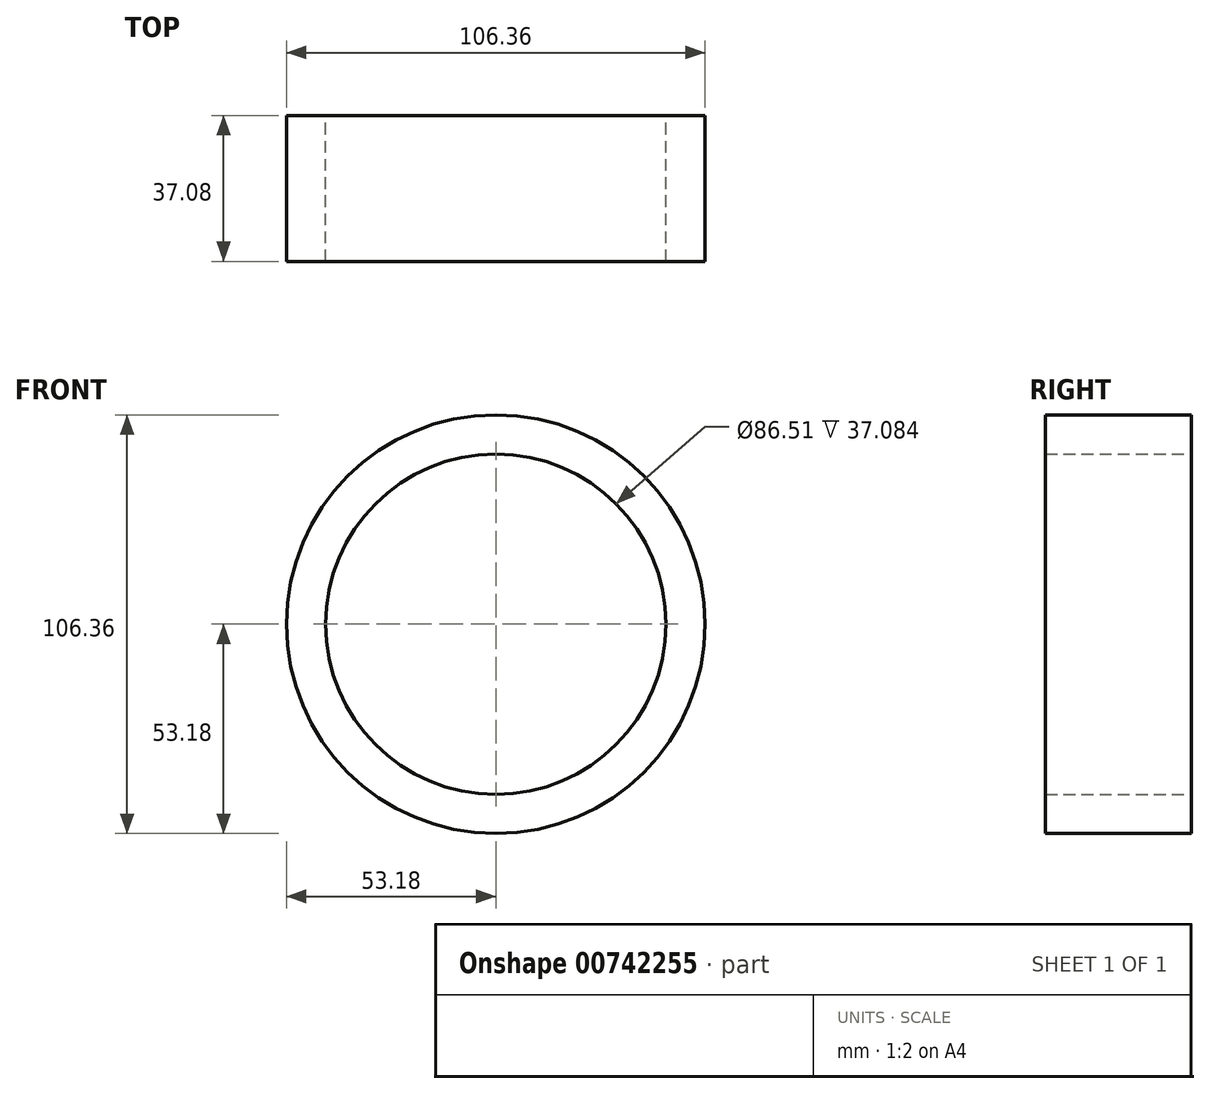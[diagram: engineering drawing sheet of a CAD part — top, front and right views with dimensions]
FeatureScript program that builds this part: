
annotation { "Feature Type Name" : "Feature", "Feature Type Description" : "" }
export const myFeature = defineFeature(function(context is Context, id is Id, definition is map)
    precondition{}
    {
        {
            var Q0;
            Q0=qCreatedBy(makeId("Front.planeOp"),FACE);
            var sketch = newSketch(context, id + "F0", { "sketchPlane" : qUnion([Q0])});
            skCircle(sketch, "E0", {"center": v(0, 0) * mm, "radius": 53.18 * mm});
            skCircle(sketch, "E1", {"center": v(0, 0) * mm, "radius": 43.26 * mm});
            skSolve(sketch);
        }
        {
            var Q0;
            Q0=makeQuery(id+"F0.imprint","IMPRINT",FACE,{"disambiguationData":[TD([[makeQuery(id+"F0.imprint","IMPRINT",EDGE,{"derivedFrom":sQuery(id+"F0.wireOp",EDGE,"E0")}),1.0]])]});
            extrude(context, id + "F1", {"entities" : qUnion([Q0]), "depth" : 37.08 * mm, "offsetDistance" : 25.4 * mm});
        }
    });
